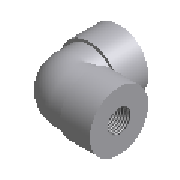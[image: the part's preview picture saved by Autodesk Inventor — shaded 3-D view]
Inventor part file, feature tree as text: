
AUTODESK INVENTOR PART (.ipt)
format: ipt  version: 2025 (Build 290162000, 162)  size: 273,920 bytes
history: native  units: mm (DEFAULTED — no unit token found)
features: other x6, revolve x4
ambient origin geometry x8: Origin, YZ Plane, XZ Plane, XY Plane, X Axis, Y Axis, Z Axis, Center Point
bodies: Solid1 (feature_tree)
feature tree (10):
  revolve  "Revolve1"  [1 undecoded]
  revolve  "Revolve2"  [1 undecoded]
  revolve  "Revolve3"  [1 undecoded]
  revolve  "Revolve4"  [1 undecoded]
  other  "Work Axis1"
  other  "Work Point1"
  other  "Work Point2"
  other  "Work Axis2"
  other  "Work Point3"
  other  "Work Point4"
note: 4 required parameter values undecoded (feature->parameter linkage not recoverable at this tier; creation-order binding heuristic only, values carry confidence <= 0.55)
